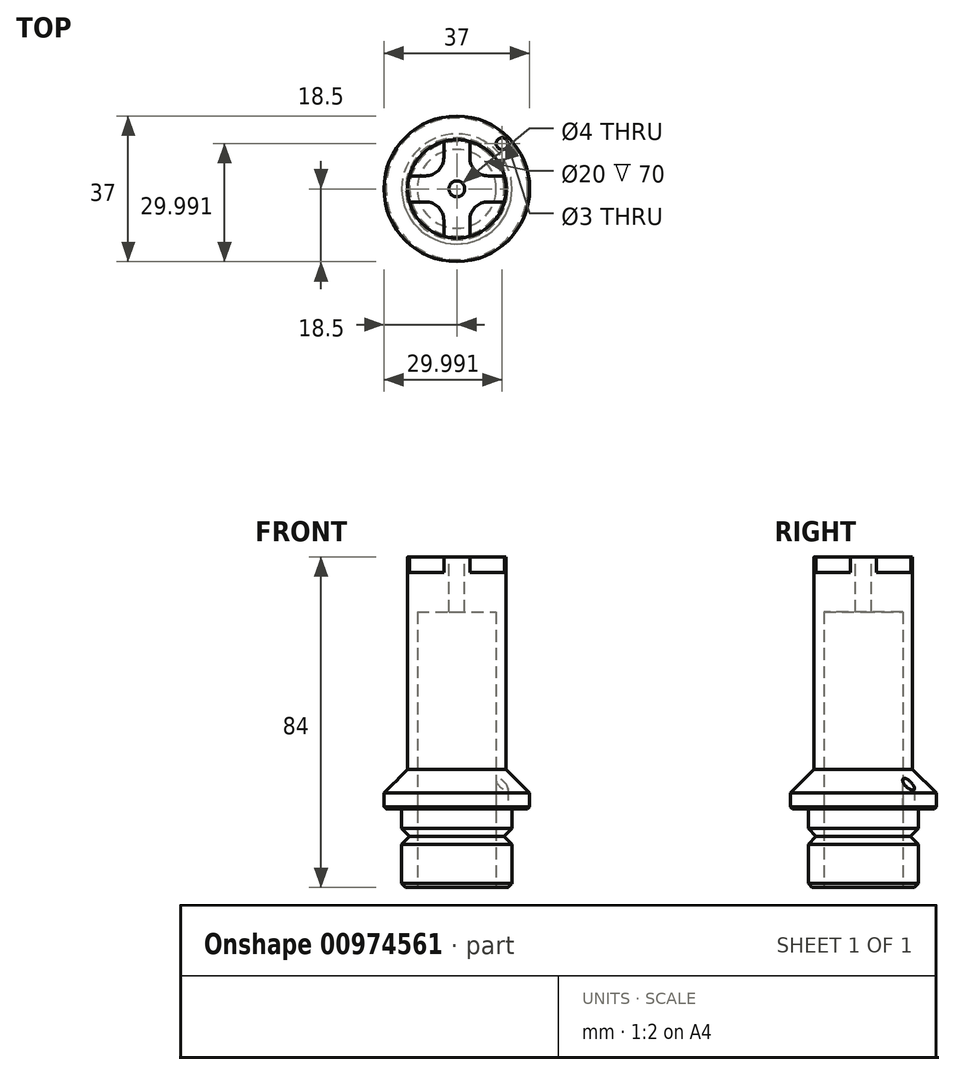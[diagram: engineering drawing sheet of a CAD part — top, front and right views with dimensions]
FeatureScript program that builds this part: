
annotation { "Feature Type Name" : "Feature", "Feature Type Description" : "" }
export const myFeature = defineFeature(function(context is Context, id is Id, definition is map)
    precondition{}
    {
        {
            var Q0;
            Q0=qCreatedBy(makeId("Top.planeOp"),FACE);
            var sketch = newSketch(context, id + "F0", { "sketchPlane" : qUnion([Q0])});
            skCircle(sketch, "E0", {"center": v(0, 0) * mm, "radius": 14 * mm});
            skSolve(sketch);
        }
        {
            var Q0;
            Q0 = qSketchRegion(id + "F0", true);
            extrude(context, id + "F1", {"entities" : qUnion([Q0]), "depth" : 80 * mm, "offsetDistance" : 25 * mm});
        }
        {
            var Q0;
            Q0=makeQuery(id+"F1.opExtrude","CAP_FACE",FACE,{"disambiguationData":[OSD([sQuery(id+"F0.wireOp",EDGE,"E0")])],"isStart":true});
            cPlane(context, id + "F2", {"entities" : qUnion([Q0]), "cplaneType" : CPlaneType.OFFSET, "offset" : 20 * mm, "oppositeDirection" : true, "width" : 150 * mm, "height" : 150 * mm});
        }
        {
            var Q0;
            Q0=qCreatedBy(id+"F2.planeOp",FACE);
            var sketch = newSketch(context, id + "F3", { "sketchPlane" : qUnion([Q0])});
            skCircle(sketch, "E1", {"center": v(0, 0) * mm, "radius": 18.5 * mm});
            skSolve(sketch);
        }
        {
            var Q0;
            Q0 = qSketchRegion(id + "F3", true);
            var Q1;
            Q1=makeQuery(id+"F1.opExtrude","CAP_FACE",FACE,{"disambiguationData":[OSD([sQuery(id+"F0.wireOp",EDGE,"E0")])],"isStart":false});
            extrude(context, id + "F4", {"entities" : qUnion([Q0]), "operationType" : NewBodyOperationType.ADD, "oppositeDirection" : true, "depth" : 4 * mm, "endBoundEntityFace" : qUnion([Q1]), "offsetDistance" : 25 * mm});
        }
        {
            var Q0;
            Q0=qCreatedBy(makeId("Front.planeOp"),FACE);
            var sketch = newSketch(context, id + "F5", { "sketchPlane" : qUnion([Q0])});
            skLineSegment(sketch, "E2", {"start": v(14, 22) * mm, "end": v(14, 0) * mm, "construction": true});
            skLineSegment(sketch, "E3", {"start": v(-14, 0) * mm, "end": v(-14, 20) * mm, "construction": true});
            skLineSegment(sketch, "E4", {"start": v(25.58, 12.5) * mm, "end": v(-25.75, 12.5) * mm, "construction": true});
            skLineSegment(sketch, "E5", {"start": v(41.3, 13) * mm, "end": v(-31.16, 13) * mm, "construction": true});
            skLineSegment(sketch, "E6", {"start": v(12, 13) * mm, "end": v(14, 11) * mm});
            skLineSegment(sketch, "E7", {"start": v(14, 11) * mm, "end": v(14, 15) * mm});
            skLineSegment(sketch, "E8", {"start": v(14, 15) * mm, "end": v(12, 13) * mm});
            skLineSegment(sketch, "E9", {"start": v(0, 0) * mm, "end": v(0, 30.65) * mm});
            skSolve(sketch);
        }
        {
            var Q0;
            Q0 = qSketchRegion(id + "F5", true);
            var Q1;
            Q1=sQuery(id+"F5.wireOp",EDGE,"E9");
            revolve(context, id + "F6", {"operationType" : NewBodyOperationType.REMOVE, "surfaceOperationType" : NewSurfaceOperationType.NEW, "entities" : qUnion([Q0]), "axis" : qUnion([Q1]), "revolveType" : RevolveType.FULL});
        }
        {
            var Q0;
            Q0=makeQuery(id+"F1.opExtrude","CAP_FACE",FACE,{"disambiguationData":[OSD([sQuery(id+"F0.wireOp",EDGE,"E0")])],"isStart":false});
            var sketch = newSketch(context, id + "F7", { "sketchPlane" : qUnion([Q0])});
            skLineSegment(sketch, "E10", {"start": v(-3.3, 0) * mm, "end": v(-3.3, 13.6) * mm});
            skLineSegment(sketch, "E11", {"start": v(3.3, 13.6) * mm, "end": v(3.3, 0) * mm});
            skArc(sketch, "E12.0", {"start": v(3.3, 13.6) * mm, "mid": v(0, 14) * mm, "end": v(-3.3, 13.6) * mm});
            skLineSegment(sketch, "E13.1.0", {"start": v(0, -3.3) * mm, "end": v(-13.6, -3.3) * mm});
            skArc(sketch, "E13.1.1", {"start": v(-13.6, 3.3) * mm, "mid": v(-14, 0) * mm, "end": v(-13.6, -3.3) * mm});
            skLineSegment(sketch, "E13.1.2", {"start": v(-13.6, 3.3) * mm, "end": v(0, 3.3) * mm});
            skLineSegment(sketch, "E13.2.0", {"start": v(3.3, 0) * mm, "end": v(3.3, -13.6) * mm});
            skArc(sketch, "E13.2.1", {"start": v(-3.3, -13.6) * mm, "mid": v(0, -14) * mm, "end": v(3.3, -13.6) * mm});
            skLineSegment(sketch, "E13.2.2", {"start": v(-3.3, -13.6) * mm, "end": v(-3.3, 0) * mm});
            skLineSegment(sketch, "E13.3.0", {"start": v(0, 3.3) * mm, "end": v(13.6, 3.3) * mm});
            skArc(sketch, "E13.3.1", {"start": v(13.6, -3.3) * mm, "mid": v(14, 0) * mm, "end": v(13.6, 3.3) * mm});
            skLineSegment(sketch, "E13.3.2", {"start": v(13.6, -3.3) * mm, "end": v(0, -3.3) * mm});
            skSolve(sketch);
        }
        {
            var Q0;
            Q0 = qSketchRegion(id + "F7", true);
            extrude(context, id + "F8", {"entities" : qUnion([Q0]), "operationType" : NewBodyOperationType.ADD, "depth" : 4 * mm, "offsetDistance" : 25 * mm});
        }
        {
            var Q0;
            Q0=makeQuery(id+"F8.opExtrude","SWEPT_EDGE",EDGE,{"disambiguationData":[OSD([sQuery(id+"F7.wireOp",EDGE,"E10"),sQuery(id+"F7.wireOp",EDGE,"E13.1.2")])]});
            var Q1;
            Q1=makeQuery(id+"F8.opExtrude","SWEPT_EDGE",EDGE,{"disambiguationData":[OSD([sQuery(id+"F7.wireOp",EDGE,"E11"),sQuery(id+"F7.wireOp",EDGE,"E13.3.0")])]});
            var Q2;
            Q2=makeQuery(id+"F8.opExtrude","SWEPT_EDGE",EDGE,{"disambiguationData":[OSD([sQuery(id+"F7.wireOp",EDGE,"E13.2.0"),sQuery(id+"F7.wireOp",EDGE,"E13.3.2")])]});
            var Q3;
            Q3=makeQuery(id+"F8.opExtrude","SWEPT_EDGE",EDGE,{"disambiguationData":[OSD([sQuery(id+"F7.wireOp",EDGE,"E13.1.0"),sQuery(id+"F7.wireOp",EDGE,"E13.2.2")])]});
            fillet(context, id + "F9", {"entities" : qUnion([Q0, Q1, Q2, Q3]), "radius" : (9.4 / 2) * mm, "tangentPropagation" : true, "allowEdgeOverflow" : false});
        }
        {
            var Q0;
            Q0=makeQuery(id+"F8.opExtrude","CAP_FACE",FACE,{"disambiguationData":[OSD([sQuery(id+"F7.wireOp",EDGE,"E10"),sQuery(id+"F7.wireOp",EDGE,"E11"),sQuery(id+"F7.wireOp",EDGE,"E12.0"),sQuery(id+"F7.wireOp",EDGE,"E13.1.0"),sQuery(id+"F7.wireOp",EDGE,"E13.1.1"),sQuery(id+"F7.wireOp",EDGE,"E13.1.2"),sQuery(id+"F7.wireOp",EDGE,"E13.2.0"),sQuery(id+"F7.wireOp",EDGE,"E13.2.1"),sQuery(id+"F7.wireOp",EDGE,"E13.2.2"),sQuery(id+"F7.wireOp",EDGE,"E13.3.0"),sQuery(id+"F7.wireOp",EDGE,"E13.3.1"),sQuery(id+"F7.wireOp",EDGE,"E13.3.2")])],"isStart":false});
            var sketch = newSketch(context, id + "F10", { "sketchPlane" : qUnion([Q0])});
            skCircle(sketch, "E14", {"center": v(0, 0) * mm, "radius": 2 * mm});
            skSolve(sketch);
        }
        {
            var Q0;
            Q0 = qSketchRegion(id + "F10", true);
            extrude(context, id + "F11", {"entities" : qUnion([Q0]), "operationType" : NewBodyOperationType.REMOVE, "endBound" : BoundingType.THROUGH_ALL, "oppositeDirection" : true, "depth" : 25 * mm, "offsetDistance" : 25 * mm});
        }
        {
            var Q0;
            Q0=makeQuery(id+"F1.opExtrude","CAP_FACE",FACE,{"disambiguationData":[OSD([sQuery(id+"F0.wireOp",EDGE,"E0")])],"isStart":true});
            var sketch = newSketch(context, id + "F12", { "sketchPlane" : qUnion([Q0])});
            skCircle(sketch, "E15", {"center": v(0, 0) * mm, "radius": 10 * mm});
            skSolve(sketch);
        }
        {
            var Q0;
            Q0=makeQuery(id+"F12.imprint","IMPRINT",FACE,{"disambiguationData":[TD([[makeQuery(id+"F12.imprint","IMPRINT",EDGE,{"derivedFrom":sQuery(id+"F12.wireOp",EDGE,"E15")}),1.0]])]});
            var Q1;
            {var subQ0=sQuery(id+"F0.wireOp",EDGE,"E0");Q1=makeQuery(id+"F8.boolean.opBoolean","SPLIT",FACE,{"disambiguationData":[TD([makeQuery(id+"F8.opExtrude","SWEPT_FACE",FACE,{"disambiguationData":[OSD([sQuery(id+"F7.wireOp",EDGE,"E13.1.0")])]})])],"derivedFrom":makeQuery(id+"F1.opExtrude","CAP_FACE",FACE,{"disambiguationData":[OSD([subQ0])],"isStart":false})});}
            var Q2;
            Q2 = qSketchRegion(id + "F12", true);
            extrude(context, id + "F13", {"entities" : qUnion([Q0, Q1, Q2]), "operationType" : NewBodyOperationType.REMOVE, "oppositeDirection" : true, "depth" : 70 * mm, "offsetDistance" : 25 * mm});
        }
        {
            var Q0;
            Q0=makeQuery(id+"F1.opExtrude","CAP_EDGE",EDGE,{"disambiguationData":[OSD([sQuery(id+"F0.wireOp",EDGE,"E0")])],"isStart":true});
            chamfer(context, id + "F14", {"entities" : qUnion([Q0]), "width" : 1 * mm, "tangentPropagation" : true});
        }
        {
            var Q0;
            Q0=makeQuery(id+"F4.opExtrude","CAP_EDGE",EDGE,{"disambiguationData":[OSD([sQuery(id+"F3.wireOp",EDGE,"E1")])],"isStart":true});
            chamfer(context, id + "F15", {"entities" : qUnion([Q0]), "width" : 0.5 * mm, "tangentPropagation" : true});
        }
        {
            var Q0;
            Q0=makeQuery(id+"F4.opExtrude","CAP_FACE",FACE,{"disambiguationData":[OSD([sQuery(id+"F3.wireOp",EDGE,"E1")])],"isStart":true});
            var sketch = newSketch(context, id + "F16", { "sketchPlane" : qUnion([Q0])});
            skCircle(sketch, "E16", {"center": v(0, 0) * mm, "radius": 16.25 * mm, "construction": true});
            skLineSegment(sketch, "E17", {"start": v(0, 0) * mm, "end": v(49.27, -49.27) * mm, "construction": true});
            skCircle(sketch, "E18", {"center": v(11.5, -11.5) * mm, "radius": 1.5 * mm});
            skSolve(sketch);
        }
        {
            var Q0;
            Q0 = qSketchRegion(id + "F16", true);
            extrude(context, id + "F17", {"entities" : qUnion([Q0]), "operationType" : NewBodyOperationType.REMOVE, "oppositeDirection" : true, "depth" : 25 * mm, "offsetDistance" : 25 * mm});
        }
        {
            var Q0;
            Q0=makeQuery(id+"F8.opExtrude","CAP_FACE",FACE,{"disambiguationData":[OSD([sQuery(id+"F7.wireOp",EDGE,"E10"),sQuery(id+"F7.wireOp",EDGE,"E11"),sQuery(id+"F7.wireOp",EDGE,"E12.0"),sQuery(id+"F7.wireOp",EDGE,"E13.1.0"),sQuery(id+"F7.wireOp",EDGE,"E13.1.1"),sQuery(id+"F7.wireOp",EDGE,"E13.1.2"),sQuery(id+"F7.wireOp",EDGE,"E13.2.0"),sQuery(id+"F7.wireOp",EDGE,"E13.2.1"),sQuery(id+"F7.wireOp",EDGE,"E13.2.2"),sQuery(id+"F7.wireOp",EDGE,"E13.3.0"),sQuery(id+"F7.wireOp",EDGE,"E13.3.1"),sQuery(id+"F7.wireOp",EDGE,"E13.3.2")])],"isStart":false});
            var sketch = newSketch(context, id + "F18", { "sketchPlane" : qUnion([Q0])});
            skCircle(sketch, "E19", {"center": v(0, 0) * mm, "radius": 12.5 * mm});
            skCircle(sketch, "E20.0", {"center": v(0, 0) * mm, "radius": 14 * mm});
            skSolve(sketch);
        }
        {
            var Q0;
            Q0 = qSketchRegion(id + "F18", true);
            var Q1;
            Q1=makeQuery(id+"F4.opExtrude","CAP_FACE",FACE,{"disambiguationData":[OSD([sQuery(id+"F3.wireOp",EDGE,"E1")])],"isStart":false});
            extrude(context, id + "F19", {"entities" : qUnion([Q0]), "operationType" : NewBodyOperationType.REMOVE, "endBound" : BoundingType.UP_TO_SURFACE, "oppositeDirection" : true, "depth" : 25 * mm, "endBoundEntityFace" : qUnion([Q1]), "offsetDistance" : 25 * mm});
        }
        {
            var Q0;
            Q0=makeQuery(id+"F19.boolean.opBoolean","COPY",EDGE,{"derivedFrom":makeQuery(id+"F19.opExtrude","CAP_EDGE",EDGE,{"disambiguationData":[OSD([sQuery(id+"F18.wireOp",EDGE,"E19")])],"isStart":false})});
            chamfer(context, id + "F20", {"entities" : qUnion([Q0]), "width" : 6 * mm, "tangentPropagation" : true});
        }
    });
